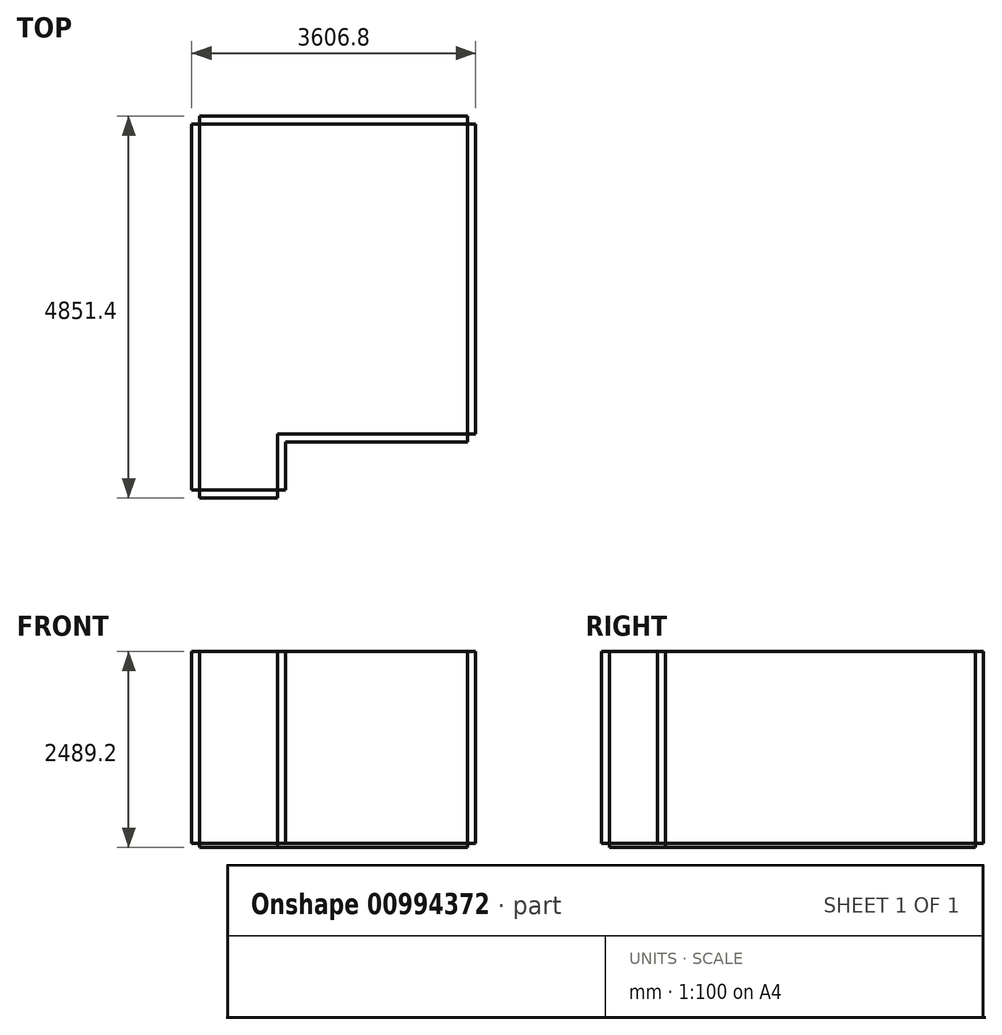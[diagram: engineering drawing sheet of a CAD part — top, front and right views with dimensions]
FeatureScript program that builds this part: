
annotation { "Feature Type Name" : "Feature", "Feature Type Description" : "" }
export const myFeature = defineFeature(function(context is Context, id is Id, definition is map)
    precondition{}
    {
        {
            var Q0;
            Q0=qCreatedBy(makeId("Top.planeOp"),FACE);
            var sketch = newSketch(context, id + "F0", { "sketchPlane" : qUnion([Q0])});
            skLineSegment(sketch, "E0", {"start": v(1701.8, 1968.5) * mm, "end": v(1701.8, -1968.5) * mm});
            skLineSegment(sketch, "E1", {"start": v(1701.8, -1968.5) * mm, "end": v(-1701.8, -1968.5) * mm});
            skLineSegment(sketch, "E2", {"start": v(-1701.8, -1968.5) * mm, "end": v(-1701.8, 1968.5) * mm});
            skLineSegment(sketch, "E3", {"start": v(-1701.8, 1968.5) * mm, "end": v(1701.8, 1968.5) * mm});
            skLineSegment(sketch, "E4", {"start": v(-1701.8, -1968.5) * mm, "end": v(-1701.8, -2679.7) * mm});
            skLineSegment(sketch, "E5", {"start": v(-1701.8, -2679.7) * mm, "end": v(-711.2, -2679.7) * mm});
            skLineSegment(sketch, "E6", {"start": v(-711.2, -2679.7) * mm, "end": v(-711.2, -1968.5) * mm});
            skSolve(sketch);
        }
        {
            var Q0;
            Q0=makeQuery(id+"F0.imprint","IMPRINT",FACE,{"disambiguationData":[TD([[makeQuery(id+"F0.imprint","IMPRINT",EDGE,{"derivedFrom":sQuery(id+"F0.wireOp",EDGE,"E0")}),-1.0]])]});
            var Q1;
            {var subQ0=sQuery(id+"F0.wireOp",EDGE,"E4");Q1=makeQuery(id+"F0.imprint","IMPRINT",FACE,{"disambiguationData":[TD([[makeQuery(id+"F0.imprint","IMPRINT",EDGE,{"derivedFrom":subQ0}),1.0]])]});}
            extrude(context, id + "F1", {"entities" : qUnion([Q0, Q1]), "depth" : 50.8 * mm, "offsetDistance" : 25.4 * mm});
        }
        {
            var Q0;
            Q0=makeQuery(id+"F1.opExtrude","CAP_FACE",FACE,{"disambiguationData":[OSD([sQuery(id+"F0.wireOp",EDGE,"E0"),sQuery(id+"F0.wireOp",EDGE,"E1"),sQuery(id+"F0.wireOp",EDGE,"E2"),sQuery(id+"F0.wireOp",EDGE,"E3"),sQuery(id+"F0.wireOp",EDGE,"E4"),sQuery(id+"F0.wireOp",EDGE,"E5"),sQuery(id+"F0.wireOp",EDGE,"E6")])],"isStart":false});
            var sketch = newSketch(context, id + "F2", { "sketchPlane" : qUnion([Q0])});
            skLineSegment(sketch, "E7", {"start": v(1701.8, 1968.5) * mm, "end": v(1701.8, 2070.1) * mm});
            skLineSegment(sketch, "E8", {"start": v(1701.8, 2070.1) * mm, "end": v(-1701.8, 2070.1) * mm});
            skLineSegment(sketch, "E9", {"start": v(-1701.8, 2070.1) * mm, "end": v(-1701.8, 1968.5) * mm});
            skLineSegment(sketch, "E10", {"start": v(-1701.8, 1968.5) * mm, "end": v(-1803.4, 1968.5) * mm});
            skLineSegment(sketch, "E11", {"start": v(-1803.4, 1968.5) * mm, "end": v(-1803.4, -2679.7) * mm});
            skLineSegment(sketch, "E12", {"start": v(-1803.4, -2679.7) * mm, "end": v(-1701.8, -2679.7) * mm});
            skLineSegment(sketch, "E13", {"start": v(-1701.8, -2679.7) * mm, "end": v(-1701.8, -2781.3) * mm});
            skLineSegment(sketch, "E14", {"start": v(-1701.8, -2781.3) * mm, "end": v(-711.2, -2781.3) * mm});
            skLineSegment(sketch, "E15", {"start": v(-711.2, -2781.3) * mm, "end": v(-711.2, -2679.7) * mm});
            skLineSegment(sketch, "E16", {"start": v(-711.2, -2679.7) * mm, "end": v(-609.6, -2679.7) * mm});
            skLineSegment(sketch, "E17", {"start": v(1701.8, 1968.5) * mm, "end": v(1803.4, 1968.5) * mm});
            skLineSegment(sketch, "E18", {"start": v(1803.4, 1968.5) * mm, "end": v(1803.4, -1968.5) * mm});
            skLineSegment(sketch, "E19", {"start": v(1803.4, -1968.5) * mm, "end": v(1701.8, -1968.5) * mm});
            skLineSegment(sketch, "E20", {"start": v(1701.8, -1968.5) * mm, "end": v(1701.8, -2070.1) * mm});
            skLineSegment(sketch, "E21", {"start": v(1701.8, -2070.1) * mm, "end": v(-609.6, -2070.1) * mm});
            skLineSegment(sketch, "E22", {"start": v(-609.6, -2070.1) * mm, "end": v(-609.6, -1968.5) * mm});
            skLineSegment(sketch, "E23", {"start": v(-609.6, -2070.1) * mm, "end": v(-609.6, -2679.7) * mm});
            skSolve(sketch);
        }
        {
            var Q0;
            Q0=makeQuery(id+"F2.imprint","IMPRINT",FACE,{"disambiguationData":[TD([[makeQuery(id+"F2.imprint","IMPRINT",EDGE,{"derivedFrom":sQuery(id+"F2.wireOp",EDGE,"E7")}),1.0]])]});
            var Q1;
            Q1=makeQuery(id+"F2.imprint","IMPRINT",FACE,{"disambiguationData":[TD([[makeQuery(id+"F2.imprint","IMPRINT",EDGE,{"derivedFrom":sQuery(id+"F2.wireOp",EDGE,"E13")}),1.0]])]});
            var Q2;
            Q2=makeQuery(id+"F2.imprint","IMPRINT",FACE,{"disambiguationData":[TD([[makeQuery(id+"F2.imprint","IMPRINT",EDGE,{"derivedFrom":sQuery(id+"F2.wireOp",EDGE,"E16")}),1.0]])]});
            var Q3;
            {var subQ0=sQuery(id+"F2.wireOp",EDGE,"E20");Q3=makeQuery(id+"F2.imprint","IMPRINT",FACE,{"disambiguationData":[TD([[makeQuery(id+"F2.imprint","IMPRINT",EDGE,{"derivedFrom":subQ0}),-1.0]])]});}
            var Q4;
            Q4=makeQuery(id+"F2.imprint","IMPRINT",FACE,{"disambiguationData":[TD([[makeQuery(id+"F2.imprint","IMPRINT",EDGE,{"derivedFrom":sQuery(id+"F2.wireOp",EDGE,"E17")}),-1.0]])]});
            var Q5;
            Q5=makeQuery(id+"F2.imprint","IMPRINT",FACE,{"disambiguationData":[TD([[makeQuery(id+"F2.imprint","IMPRINT",EDGE,{"derivedFrom":sQuery(id+"F2.wireOp",EDGE,"E10")}),1.0]])]});
            extrude(context, id + "F3", {"entities" : qUnion([Q0, Q1, Q2, Q3, Q4, Q5]), "depth" : 2438.4 * mm, "offsetDistance" : 25.4 * mm});
        }
    });
